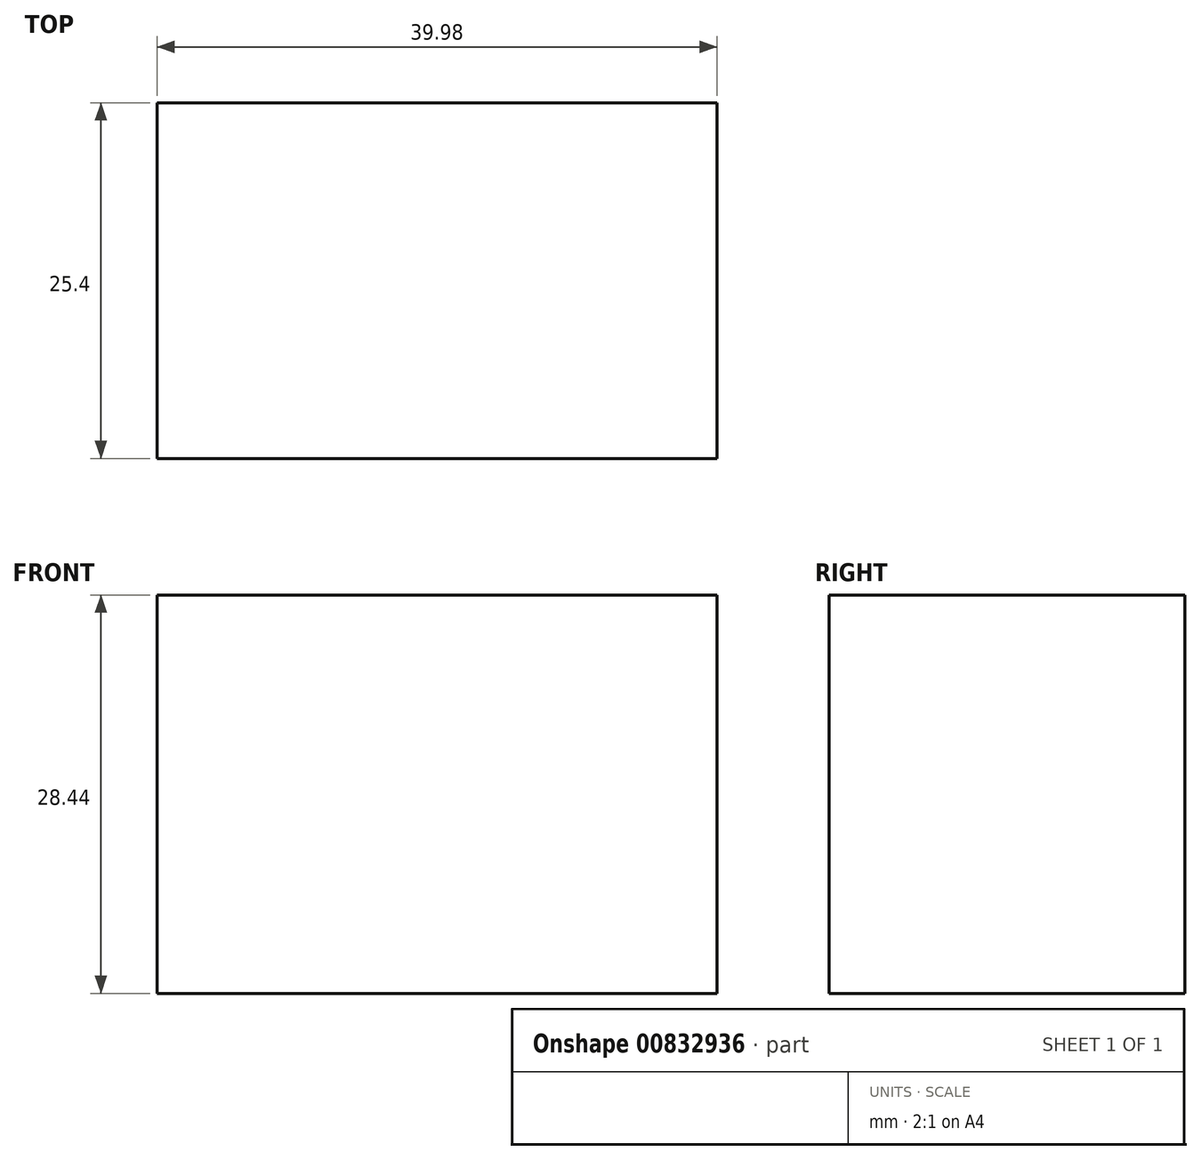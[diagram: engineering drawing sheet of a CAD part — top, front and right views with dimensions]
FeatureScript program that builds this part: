
annotation { "Feature Type Name" : "Feature", "Feature Type Description" : "" }
export const myFeature = defineFeature(function(context is Context, id is Id, definition is map)
    precondition{}
    {
        {
            var Q0;
            Q0=qCreatedBy(makeId("Front.planeOp"),FACE);
            var sketch = newSketch(context, id + "F0", { "sketchPlane" : qUnion([Q0])});
            skLineSegment(sketch, "E0.bottom", {"start": v(-149.92, -45.45) * mm, "end": v(-109.94, -45.45) * mm});
            skLineSegment(sketch, "E0.top", {"start": v(-149.92, -73.89) * mm, "end": v(-109.94, -73.89) * mm});
            skLineSegment(sketch, "E0.left", {"start": v(-149.92, -45.45) * mm, "end": v(-149.92, -73.89) * mm});
            skLineSegment(sketch, "E0.right", {"start": v(-109.94, -45.45) * mm, "end": v(-109.94, -73.89) * mm});
            skSolve(sketch);
        }
        {
            var Q0;
            Q0 = qSketchRegion(id + "F0", true);
            extrude(context, id + "F1", {"entities" : qUnion([Q0]), "depth" : 25.4 * mm, "offsetDistance" : 25.4 * mm});
        }
    });
